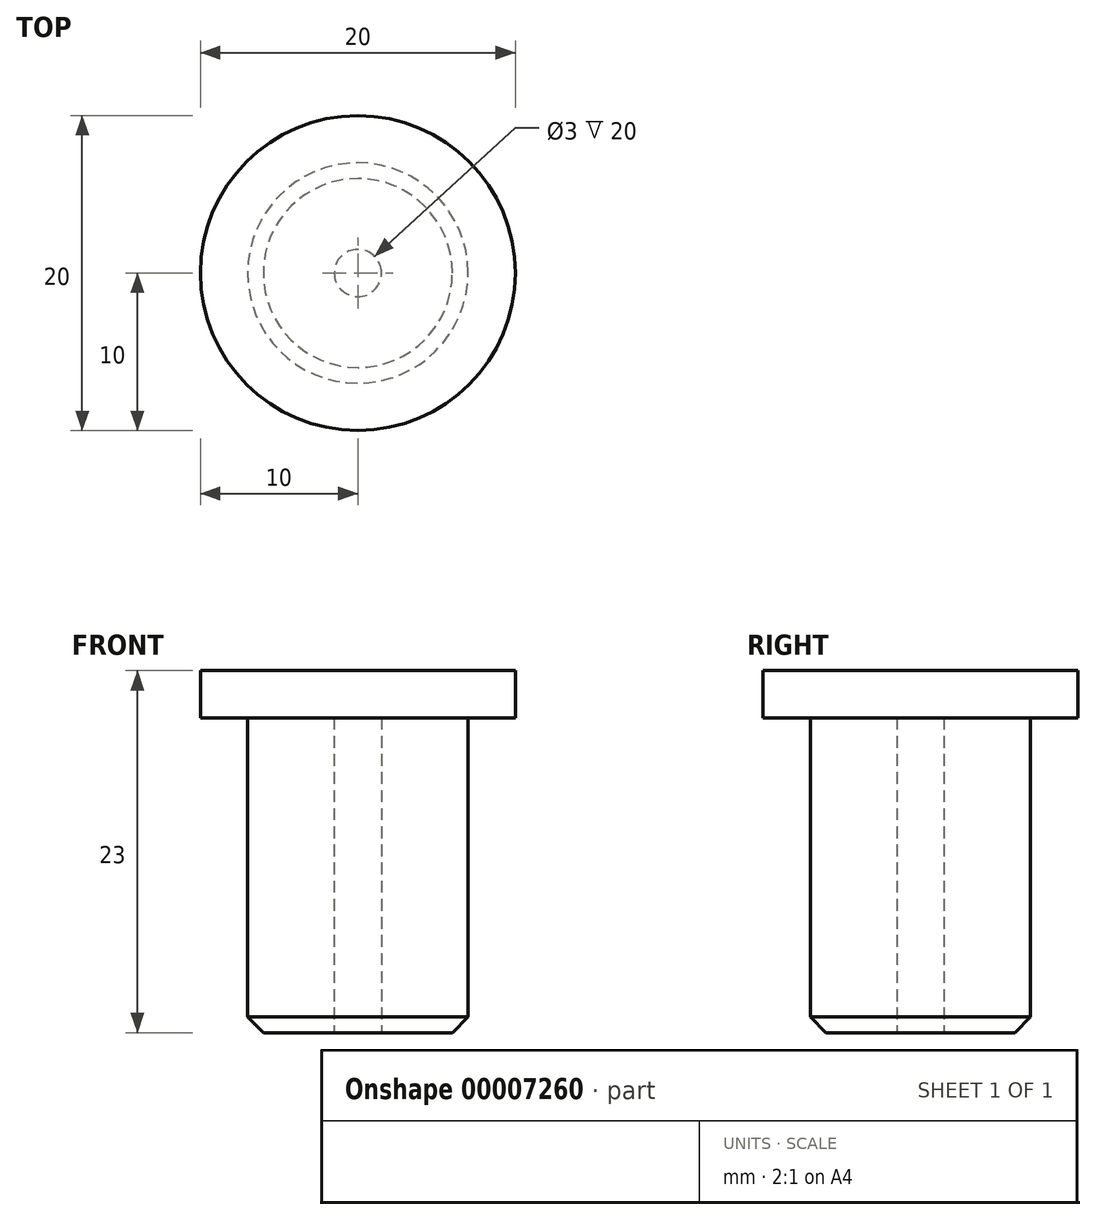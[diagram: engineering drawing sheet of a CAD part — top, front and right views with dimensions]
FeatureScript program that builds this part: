
annotation { "Feature Type Name" : "Feature", "Feature Type Description" : "" }
export const myFeature = defineFeature(function(context is Context, id is Id, definition is map)
    precondition{}
    {
        {
            var Q0;
            Q0=qCreatedBy(makeId("Front.planeOp"),FACE);
            var sketch = newSketch(context, id + "F0", { "sketchPlane" : qUnion([Q0])});
            skLineSegment(sketch, "E0", {"start": v(0, 0) * mm, "end": v(10, 0) * mm});
            skLineSegment(sketch, "E1", {"start": v(10, 0) * mm, "end": v(10, -3) * mm});
            skLineSegment(sketch, "E2", {"start": v(10, -3) * mm, "end": v(7, -3) * mm});
            skLineSegment(sketch, "E3", {"start": v(7, -3) * mm, "end": v(7, -22) * mm});
            skLineSegment(sketch, "E4", {"start": v(7, -22) * mm, "end": v(6, -23) * mm});
            skLineSegment(sketch, "E5", {"start": v(6, -23) * mm, "end": v(0, -23) * mm});
            skLineSegment(sketch, "E6", {"start": v(0, -23) * mm, "end": v(0, 0) * mm});
            skSolve(sketch);
        }
        {
            var Q0;
            Q0=makeQuery(id+"F0.imprint","IMPRINT",FACE,{"disambiguationData":[TD([[makeQuery(id+"F0.imprint","IMPRINT",EDGE,{"derivedFrom":sQuery(id+"F0.wireOp",EDGE,"E0")}),-1.0]])]});
            var Q1;
            Q1=sQuery(id+"F0.wireOp",EDGE,"E6");
            revolve(context, id + "F1", {"entities" : qUnion([Q0]), "axis" : qUnion([Q1]), "revolveType" : RevolveType.FULL});
        }
        {
            var Q0;
            Q0=makeQuery(id+"F1.opRevolve","SWEPT_FACE",FACE,{"disambiguationData":[OSD([sQuery(id+"F0.wireOp",EDGE,"E5")])]});
            var sketch = newSketch(context, id + "F2", { "sketchPlane" : qUnion([Q0])});
            skCircle(sketch, "E7", {"center": v(0, 0) * mm, "radius": 1.5 * mm});
            skSolve(sketch);
        }
        {
            var Q0;
            Q0=makeQuery(id+"F2.imprint","IMPRINT",FACE,{"disambiguationData":[TD([[makeQuery(id+"F2.imprint","IMPRINT",EDGE,{"derivedFrom":sQuery(id+"F2.wireOp",EDGE,"E7")}),1.0]])]});
            extrude(context, id + "F3", {"entities" : qUnion([Q0]), "operationType" : NewBodyOperationType.REMOVE, "oppositeDirection" : true, "depth" : 20 * mm});
        }
    });
